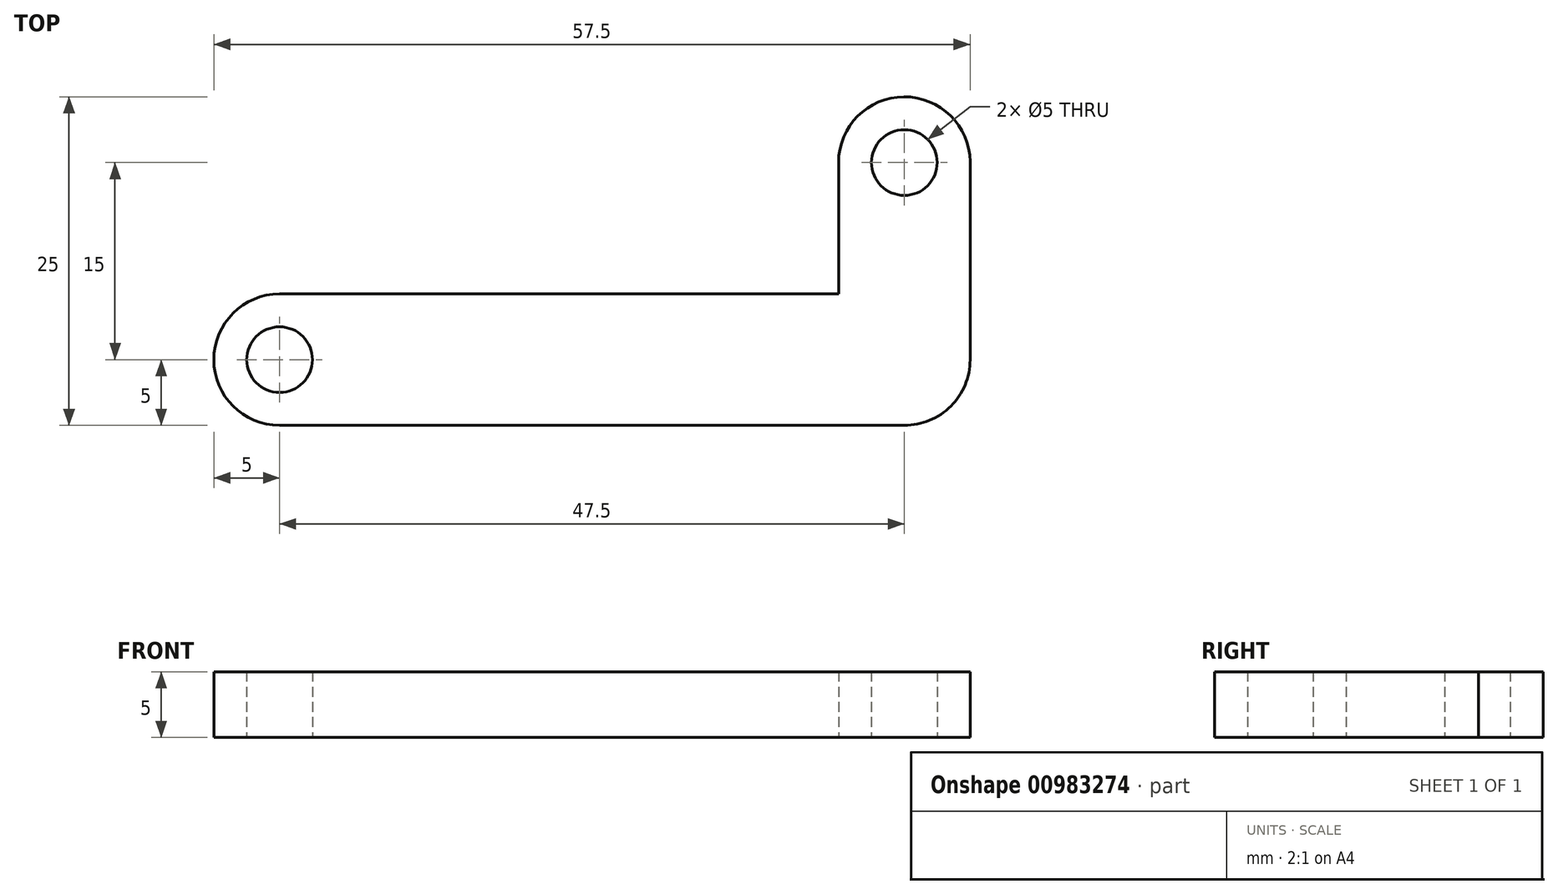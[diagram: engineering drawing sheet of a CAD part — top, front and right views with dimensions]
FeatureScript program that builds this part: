
annotation { "Feature Type Name" : "Feature", "Feature Type Description" : "" }
export const myFeature = defineFeature(function(context is Context, id is Id, definition is map)
    precondition{}
    {
        {
            var Q0;
            Q0=qCreatedBy(makeId("Top.planeOp"),FACE);
            var sketch = newSketch(context, id + "F0", { "sketchPlane" : qUnion([Q0])});
            skCircle(sketch, "E0", {"center": v(0, 0) * mm, "radius": 2.5 * mm});
            skLineSegment(sketch, "E1", {"start": v(0, -5) * mm, "end": v(47.5, -5) * mm});
            skArc(sketch, "E2", {"start": v(0, 5) * mm, "mid": v(-5, 0) * mm, "end": v(0, -5) * mm});
            skCircle(sketch, "E3", {"center": v(47.5, 15) * mm, "radius": 2.5 * mm});
            skLineSegment(sketch, "E4", {"start": v(52.5, 15.06) * mm, "end": v(52.5, 0) * mm});
            skLineSegment(sketch, "E5", {"start": v(42.5, 15) * mm, "end": v(42.5, 5) * mm});
            skLineSegment(sketch, "E6", {"start": v(0, 5) * mm, "end": v(42.5, 5) * mm});
            skArc(sketch, "E7", {"start": v(47.5, -5) * mm, "mid": v(51.04, -3.54) * mm, "end": v(52.5, 0) * mm});
            skArc(sketch, "E8", {"start": v(52.5, 15.06) * mm, "mid": v(47.47, 20) * mm, "end": v(42.5, 15) * mm});
            skSolve(sketch);
        }
        {
            var Q0;
            Q0=makeQuery(id+"F0.imprint","IMPRINT",FACE,{"disambiguationData":[TD([[makeQuery(id+"F0.imprint","IMPRINT",EDGE,{"derivedFrom":sQuery(id+"F0.wireOp",EDGE,"E0")}),-1.0]])]});
            extrude(context, id + "F1", {"entities" : qUnion([Q0]), "depth" : 5 * mm, "offsetDistance" : 25 * mm});
        }
    });
